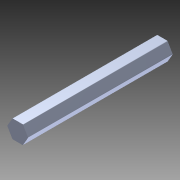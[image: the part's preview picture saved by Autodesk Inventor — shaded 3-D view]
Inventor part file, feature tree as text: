
AUTODESK INVENTOR PART (.ipt)
format: ipt  version: 2014 (Build 180170000, 170)  size: 119,296 bytes
history: native  units: in
note: dims shown in document units (in); Inventor stores cm internally (conversion verified against a paired STEP export)
features: fillet x1, other x1, extrude x1, imported_body x1, sketch x1
ambient origin geometry x8: Origin, YZ Plane, XZ Plane, XY Plane, X Axis, Y Axis, Z Axis, Center Point
bodies: Body1 (feature_tree)
feature tree (5):
  fillet  "Fillet1"  Radius=14.0in
  other  "18inShaft1"
  extrude  "Extrusion1"  [1 undecoded]
  imported_body  "Base1"
  sketch  "Sketch1"
note: 1 required parameter value undecoded (feature->parameter linkage not recoverable at this tier; creation-order binding heuristic only, values carry confidence <= 0.55)
